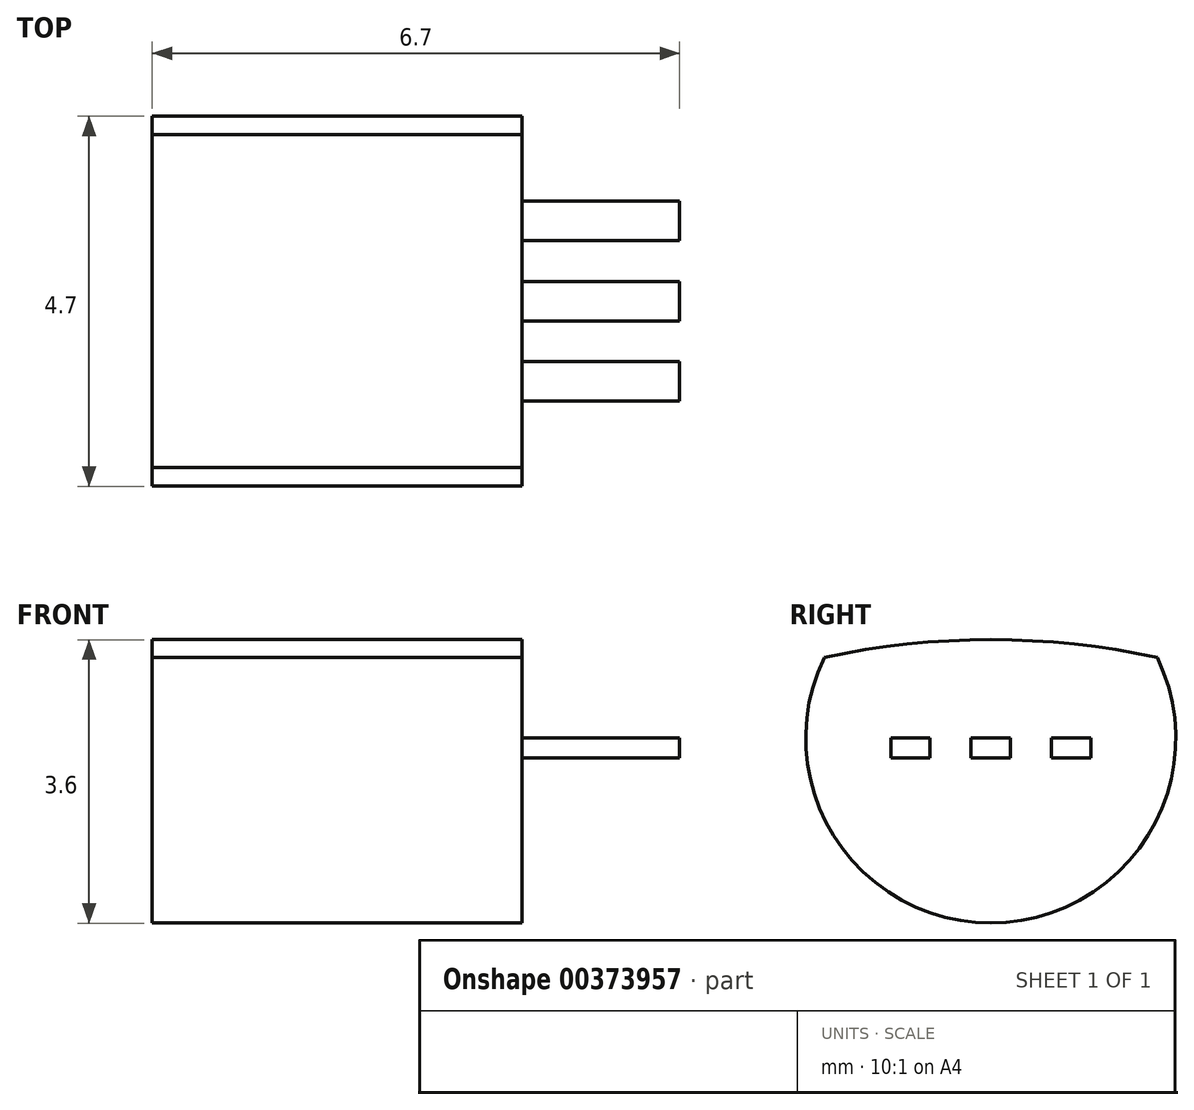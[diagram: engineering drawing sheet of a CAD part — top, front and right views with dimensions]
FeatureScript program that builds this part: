
annotation { "Feature Type Name" : "Feature", "Feature Type Description" : "" }
export const myFeature = defineFeature(function(context is Context, id is Id, definition is map)
    precondition{}
    {
        {
            var Q0;
            Q0=qCreatedBy(makeId("Right.planeOp"),FACE);
            var sketch = newSketch(context, id + "F0", { "sketchPlane" : qUnion([Q0])});
            skArc(sketch, "E0", {"start": v(9.5, 2.27) * mm, "mid": v(11.62, -1.1) * mm, "end": v(13.74, 2.27) * mm});
            skLineSegment(sketch, "E1", {"start": v(11.62, 1.24) * mm, "end": v(11.62, -7.5) * mm, "construction": true});
            skPoint(sketch, "E2", {"position": v(11.62, -1.1) * mm});
            skArc(sketch, "E3", {"start": v(13.74, 2.27) * mm, "mid": v(11.62, 2.5) * mm, "end": v(9.5, 2.27) * mm});
            skSolve(sketch);
        }
        {
            var Q0;
            Q0=qSketchRegion(id+"F0",true);
            extrude(context, id + "F1", {"entities" : qUnion([Q0]), "depth" : 4.7 * mm, "offsetDistance" : 25 * mm});
        }
        {
            var Q0;
            Q0=makeQuery(id+"F1.opExtrude","CAP_FACE",FACE,{"disambiguationData":[OSD([sQuery(id+"F0.wireOp",EDGE,"E0"),sQuery(id+"F0.wireOp",EDGE,"pQy59nGK-P0kE-zOxA-EJ2T-yzfUfhpIp4yW")])],"isStart":false});
            var sketch = newSketch(context, id + "F2", { "sketchPlane" : qUnion([Q0])});
            skLineSegment(sketch, "E4.bottom", {"start": v(10.35, 1.24) * mm, "end": v(10.85, 1.24) * mm});
            skLineSegment(sketch, "E4.top", {"start": v(10.35, 1) * mm, "end": v(10.85, 1) * mm});
            skLineSegment(sketch, "E4.left", {"start": v(10.35, 1.24) * mm, "end": v(10.35, 1) * mm});
            skLineSegment(sketch, "E4.right", {"start": v(10.85, 1.24) * mm, "end": v(10.85, 1) * mm});
            skLineSegment(sketch, "E5.bottom", {"start": v(11.37, 1.24) * mm, "end": v(11.87, 1.24) * mm});
            skLineSegment(sketch, "E5.top", {"start": v(11.37, 1) * mm, "end": v(11.87, 1) * mm});
            skLineSegment(sketch, "E5.left", {"start": v(11.37, 1.24) * mm, "end": v(11.37, 1) * mm});
            skLineSegment(sketch, "E5.right", {"start": v(11.87, 1.24) * mm, "end": v(11.87, 1) * mm});
            skLineSegment(sketch, "E6.bottom", {"start": v(12.4, 1.24) * mm, "end": v(12.9, 1.24) * mm});
            skLineSegment(sketch, "E6.top", {"start": v(12.4, 1) * mm, "end": v(12.9, 1) * mm});
            skLineSegment(sketch, "E6.left", {"start": v(12.4, 1.24) * mm, "end": v(12.4, 1) * mm});
            skLineSegment(sketch, "E6.right", {"start": v(12.9, 1.24) * mm, "end": v(12.9, 1) * mm});
            skLineSegment(sketch, "E7", {"start": v(11.62, 1.24) * mm, "end": v(11.62, -1.85) * mm, "construction": true});
            skPoint(sketch, "E7.endSnap0", {"position": v(11.62, -1.1) * mm});
            skLineSegment(sketch, "E8", {"start": v(11.62, 1.24) * mm, "end": v(8.3, 1.24) * mm, "construction": true});
            skLineSegment(sketch, "E9", {"start": v(11.62, 1.24) * mm, "end": v(14.82, 1.24) * mm, "construction": true});
            skLineSegment(sketch, "E10", {"start": v(11.62, 1.24) * mm, "end": v(11.62, 2.86) * mm, "construction": true});
            skPoint(sketch, "E10.endSnap0", {"position": v(11.62, 2.5) * mm});
            skSolve(sketch);
        }
        {
            var Q0;
            Q0=qSketchRegion(id+"F2",true);
            extrude(context, id + "F3", {"entities" : qUnion([Q0]), "depth" : 2 * mm, "offsetDistance" : 25 * mm});
        }
    });
